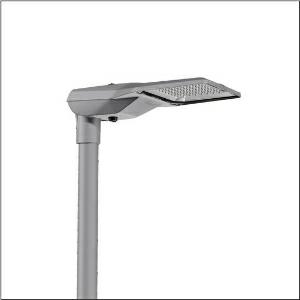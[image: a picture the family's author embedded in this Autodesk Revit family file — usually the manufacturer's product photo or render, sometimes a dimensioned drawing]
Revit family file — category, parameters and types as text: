
# Revit family: streetlight_sl_21_iq_midi___st1_0a_5xe3d41y08mb_a031
name_source: partatom
category: Lighting Fixtures
units: mm (PartAtom-declared; Revit-internal decimal feet)

## family parameters
Cut with Voids When Loaded = No
Host = Face
Light Source = No
Part Type = Normal
Room Calculation Point = No
Round Connector Dimension = Use Diameter
Shared = No

## types (1)
- --- (1 x LED, 18980 lm, 129.3 W, 4000K)
    Apparent Load = 129 VA
    CIE Flux Codes = 37 72 97 100 100
    Color Rendering = 70
    Color Temperature = 4000K
    Default Elevation = 1800 mm
    Description = Streetlight SL 21 iQ midi, mast luminaire, primary light control with lens, of PMMA, primary optical cover: cover, of toughened safety glass, transparent, light distribution: ST1.0a, light emission: direct distribution, primary light characteristic: asymmetric, installation type: post-top, side-entry, LED, High Power LED, rated luminous flux: 18.980lm, luminous efficacy: 147lm/W, light colour: 740, colour temperature: 4000K, control gear: iQ-Street Remote, D4i with power reduction, control: pre-setting: logarithmic dimming characteristic, Street-Remote, Auto-Match, Temp-Guard, Lumen-Switch, Night-Set, Smart-Wire, Light-Fading, Desk-Remote (wireless, voltage-free reading and setting of iQ features in the workshop via application-optimized NFC function/RFID function), optimised constant luminous flux control (CLO 2.0), mains connection: 230..240V, AC, 50/60Hz, start of lifetime: 129W, end of service life: 142W, reduction: 56W, luminaire housing, of diecast aluminium, powder-coated, Siteco® metallic grey (DB 702S), corrosivity category C5 mid according to DIN EN ISO 12944, please order mast flange separately, inclination adjustable: 0°, 5°, 10°, 15°, sealing non-destructively replaceable, multi-level sealing system, length: 644mm, width: 335mm, height: 110mm, mast flange for spigot size: 42mm (side-entry): 5XC10008XM4, 60/48mm (side-entry/post-top): 5XC10108XM2, 76/60mm (side-entry/post-top): 5XC10108XM1, mounting height: 4..8m, Smart Interface below and above, protection rating (complete): IP66, insulation class (complete): insulation class II (safety insulation), certification: CE, ENEC, ENEC+, VDE, impact resistance: IK10, permissible operating ambient temperature for outdoor applications: -40..+50°C, standard-compliant lighting for roads and squares, packaging unit: 1 piece

Light Distribution: ST1.0a
    Height = 111 mm
    Lamp = 1 x LED
    Lamp Light Flux = 18980 lm
    Lamp Power = 129.3 W
    Lamp count = 1
    Length = 644 mm
    Luminous efficacy = 147 lm/W
    Manufacturer = Siteco
    ModVariant = No
    Model = 5XE3D41Y08MB
    Number of Poles = 1
    OnlyDefault = Yes
    Power Factor = 1
    Product Name = Streetlight SL 21 iQ midi | ST1.0a
    Product group = mast luminaire | pylon top
    ProductGroupID = 6100
    Protection Class = Protection class II
    Protection Degree = IP 66
    RLX_Detail_Level = 1
    RLX_Emergency_Light_Flux = 0 lm
    RLX_Emergency_Type = 0
    RLX_Emergency_Type_DB = No
    RlxData = <blob elided: 27245 chars, md5=6e573f2e>
    Socket = socket
    Standby Power = 0 W
    System Light Flux = 18980 lm
    System Power = 129 W
    Type Comments = factory setting: luminous flux: 100 % | dim-lin: 254 | 672 mA
    Type Image = l_1004304.jpg
    URL = http://relux.com
    VarID = @adj_114454
    Voltage = 0 V
    Weight = 0.00 kg
    Width = 336 mm

## geometry (parser evidence)
native form markers: Blend x4, Sweep x10
no freeform markers — native parametric forms only
